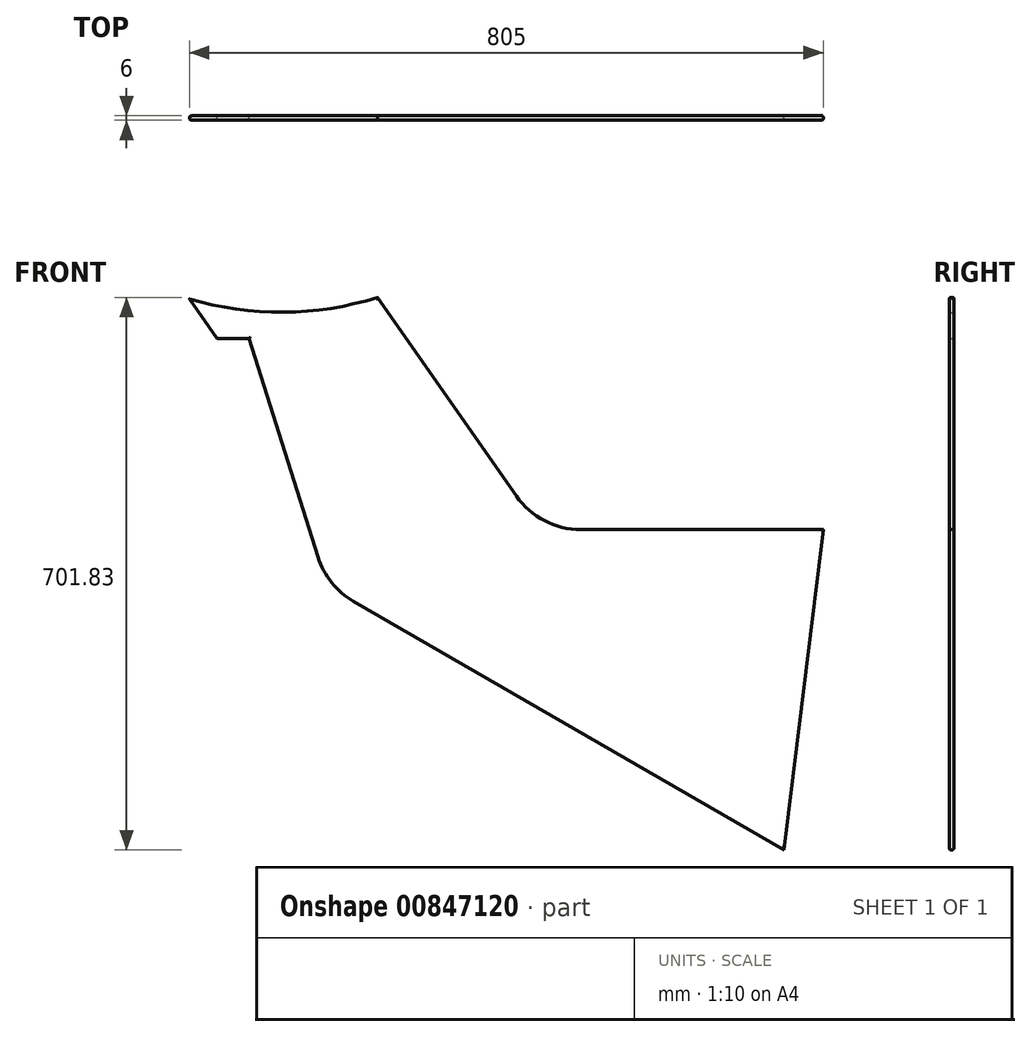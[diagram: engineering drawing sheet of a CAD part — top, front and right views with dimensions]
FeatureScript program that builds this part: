
annotation { "Feature Type Name" : "Feature", "Feature Type Description" : "" }
export const myFeature = defineFeature(function(context is Context, id is Id, definition is map)
    precondition{}
    {
        {
            var Q0;
            Q0=qCreatedBy(makeId("Front.planeOp"),FACE);
            var sketch = newSketch(context, id + "F0", { "sketchPlane" : qUnion([Q0])});
            skLineSegment(sketch, "E0", {"start": v(52.06, 0) * mm, "end": v(360, 0) * mm});
            skLineSegment(sketch, "E1", {"start": v(360, 0) * mm, "end": v(310, -406.94) * mm});
            skLineSegment(sketch, "E2", {"start": v(310, -406.94) * mm, "end": v(-236.56, -91.38) * mm});
            skLineSegment(sketch, "E3", {"start": v(-281.93, -34.85) * mm, "end": v(-369.47, 242.79) * mm});
            skLineSegment(sketch, "E4", {"start": v(-369.47, 242.79) * mm, "end": v(-409.8, 242.79) * mm});
            skLineSegment(sketch, "E5", {"start": v(-409.8, 242.79) * mm, "end": v(-445, 293.06) * mm});
            skLineSegment(sketch, "E6", {"start": v(-206.49, 294.9) * mm, "end": v(-29.86, 42.64) * mm});
            skPoint(sketch, "E7.visualSharp", {"position": v(-270.24, -71.94) * mm});
            skArc(sketch, "E7.filletArc", {"start": v(-281.93, -34.85) * mm, "mid": v(-264.55, -67.37) * mm, "end": v(-236.56, -91.38) * mm});
            skPoint(sketch, "E8.visualSharp", {"position": v(0, 0) * mm});
            skArc(sketch, "E8.filletArc", {"start": v(-29.86, 42.64) * mm, "mid": v(5.88, 11.3) * mm, "end": v(52.06, 0) * mm});
            skLineSegment(sketch, "E9", {"start": v(310, -406.94) * mm, "end": v(-167.7, -406.94) * mm, "construction": true});
            skArc(sketch, "E10", {"start": v(-445, 293.06) * mm, "mid": v(-325.6, 276.02) * mm, "end": v(-206.49, 294.9) * mm});
            skSolve(sketch);
        }
        {
            var Q0;
            Q0=makeQuery(id+"F0.imprint","IMPRINT",FACE,{"disambiguationData":[TD([[makeQuery(id+"F0.imprint","IMPRINT",EDGE,{"derivedFrom":sQuery(id+"F0.wireOp",EDGE,"E0")}),-1.0]])]});
            extrude(context, id + "F1", {"entities" : qUnion([Q0]), "depth" : 6 * mm, "offsetDistance" : 25 * mm});
        }
        {
            var Q0;
            Q0=makeQuery(id+"F1.opExtrude","CAP_FACE",FACE,{"disambiguationData":[OSD([sQuery(id+"F0.wireOp",EDGE,"E0"),sQuery(id+"F0.wireOp",EDGE,"E1"),sQuery(id+"F0.wireOp",EDGE,"E2"),sQuery(id+"F0.wireOp",EDGE,"E3"),sQuery(id+"F0.wireOp",EDGE,"E4"),sQuery(id+"F0.wireOp",EDGE,"E5"),sQuery(id+"F0.wireOp",EDGE,"E6"),sQuery(id+"F0.wireOp",EDGE,"E7.filletArc"),sQuery(id+"F0.wireOp",EDGE,"E8.filletArc"),sQuery(id+"F0.wireOp",EDGE,"E10")])],"isStart":false});
            var Q1;
            Q1=makeQuery(id+"F1.opExtrude","CAP_FACE",FACE,{"disambiguationData":[OSD([sQuery(id+"F0.wireOp",EDGE,"E0"),sQuery(id+"F0.wireOp",EDGE,"E1"),sQuery(id+"F0.wireOp",EDGE,"E2"),sQuery(id+"F0.wireOp",EDGE,"E3"),sQuery(id+"F0.wireOp",EDGE,"E4"),sQuery(id+"F0.wireOp",EDGE,"E5"),sQuery(id+"F0.wireOp",EDGE,"E6"),sQuery(id+"F0.wireOp",EDGE,"E7.filletArc"),sQuery(id+"F0.wireOp",EDGE,"E8.filletArc"),sQuery(id+"F0.wireOp",EDGE,"E10")])],"isStart":true});
            fillet(context, id + "F2", {"entities" : qUnion([Q0, Q1]), "radius" : 2 * mm, "tangentPropagation" : true, "allowEdgeOverflow" : false});
        }
    });
